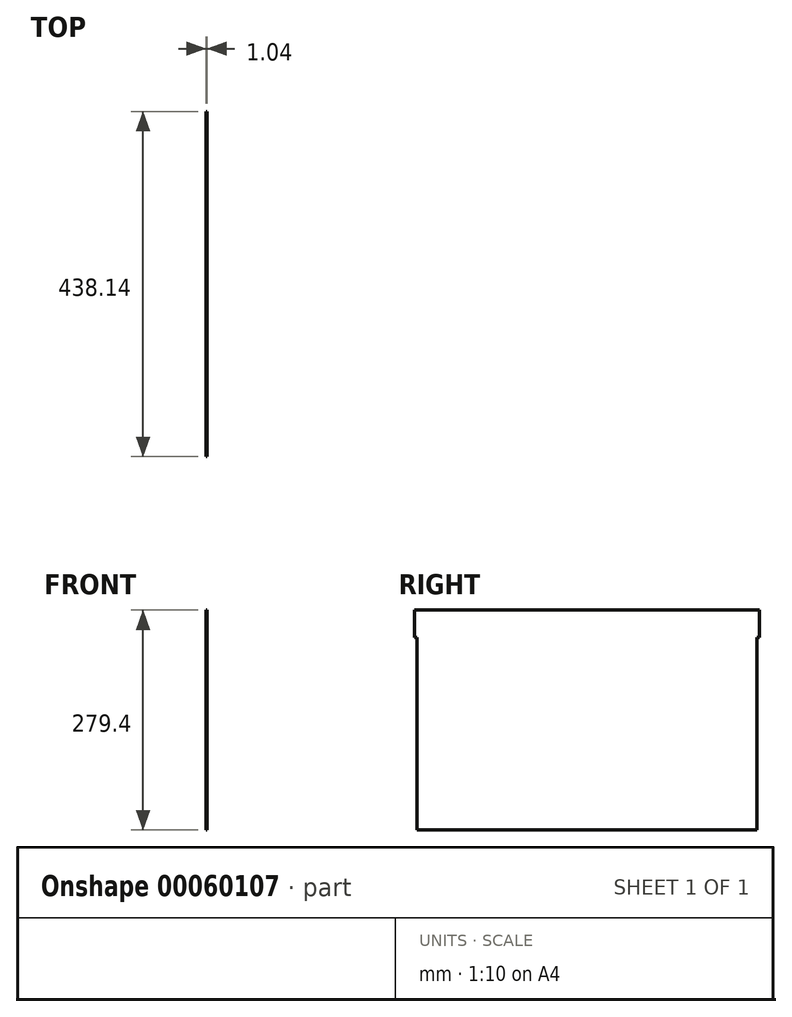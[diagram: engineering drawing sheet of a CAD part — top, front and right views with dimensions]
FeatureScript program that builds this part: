
annotation { "Feature Type Name" : "Feature", "Feature Type Description" : "" }
export const myFeature = defineFeature(function(context is Context, id is Id, definition is map)
    precondition{}
    {
        {
            var Q0;
            Q0=qCreatedBy(makeId("Right.planeOp"),FACE);
            var sketch = newSketch(context, id + "F0", { "sketchPlane" : qUnion([Q0])});
            skLineSegment(sketch, "E0", {"start": v(-219.08, 127) * mm, "end": v(219.08, 127) * mm});
            skLineSegment(sketch, "E1", {"start": v(219.07, 127) * mm, "end": v(219.07, 92.07) * mm});
            skLineSegment(sketch, "E2", {"start": v(219.07, 92.08) * mm, "end": v(215.9, 92.08) * mm});
            skLineSegment(sketch, "E3", {"start": v(215.9, 92.07) * mm, "end": v(215.9, -152.4) * mm});
            skLineSegment(sketch, "E4", {"start": v(215.9, -152.4) * mm, "end": v(-215.9, -152.4) * mm});
            skLineSegment(sketch, "E5", {"start": v(-215.9, -152.4) * mm, "end": v(-215.9, 92.07) * mm});
            skLineSegment(sketch, "E6", {"start": v(-215.9, 92.07) * mm, "end": v(-219.07, 92.07) * mm});
            skLineSegment(sketch, "E7", {"start": v(-219.07, 92.07) * mm, "end": v(-219.07, 127) * mm});
            skLineSegment(sketch, "E8", {"start": v(0, 0) * mm, "end": v(0, 127) * mm, "construction": true});
            skSolve(sketch);
        }
        {
            var Q0;
            Q0 = qSketchRegion(id + "F0", true);
            extrude(context, id + "F1", {"entities" : qUnion([Q0]), "depth" : (26 + 3 / 8) / 50.8 * mm, "hasSecondDirection" : true, "secondDirectionOppositeDirection" : true, "secondDirectionDepth" : (26 + 3 / 8) / 50.8 * mm});
        }
        {
            var Q0;
            Q0=makeQuery(id+"F1.opExtrude","SWEPT_FACE",FACE,{"disambiguationData":[OSD([sQuery(id+"F0.wireOp",EDGE,"E4")])]});
            var sketch = newSketch(context, id + "F2", { "sketchPlane" : qUnion([Q0])});
            skLineSegment(sketch, "E9.bottom", {"start": v(234.95, -215.9) * mm, "end": v(-234.95, -215.9) * mm, "construction": true});
            skLineSegment(sketch, "E9.top", {"start": v(234.95, 215.9) * mm, "end": v(-234.95, 215.9) * mm, "construction": true});
            skLineSegment(sketch, "E9.left", {"start": v(234.95, -215.9) * mm, "end": v(234.95, 215.9) * mm, "construction": true});
            skLineSegment(sketch, "E9.right", {"start": v(-234.95, -215.9) * mm, "end": v(-234.95, 215.9) * mm, "construction": true});
            skLineSegment(sketch, "E10", {"start": v(0, 0) * mm, "end": v(0, -215.9) * mm, "construction": true});
            skLineSegment(sketch, "E11", {"start": v(0, 0) * mm, "end": v(234.95, 0) * mm, "construction": true});
            skLineSegment(sketch, "E12.bottom", {"start": v(-334.96, -215.9) * mm, "end": v(-234.95, -215.9) * mm});
            skLineSegment(sketch, "E12.top", {"start": v(-334.96, 215.9) * mm, "end": v(-234.95, 215.9) * mm});
            skLineSegment(sketch, "E12.left", {"start": v(-334.96, -215.9) * mm, "end": v(-334.96, 215.9) * mm});
            skLineSegment(sketch, "E12.right", {"start": v(-234.95, -215.9) * mm, "end": v(-234.95, 215.9) * mm});
            skLineSegment(sketch, "E13.bottom", {"start": v(234.95, -215.9) * mm, "end": v(334.96, -215.9) * mm});
            skLineSegment(sketch, "E13.top", {"start": v(234.95, 215.9) * mm, "end": v(334.96, 215.9) * mm});
            skLineSegment(sketch, "E13.left", {"start": v(234.95, -215.9) * mm, "end": v(234.95, 215.9) * mm});
            skLineSegment(sketch, "E13.right", {"start": v(334.96, -215.9) * mm, "end": v(334.96, 215.9) * mm});
            skSolve(sketch);
        }
        {
            var Q0;
            Q0 = qSketchRegion(id + "F2", true);
            var Q1;
            Q1=makeQuery(id+"F1.opExtrude","SWEPT_FACE",FACE,{"disambiguationData":[OSD([sQuery(id+"F0.wireOp",EDGE,"E2")])]});
            extrude(context, id + "F3", {"entities" : qUnion([Q0]), "operationType" : NewBodyOperationType.REMOVE, "endBound" : BoundingType.UP_TO_SURFACE, "oppositeDirection" : true, "endBoundEntityFace" : qUnion([Q1]), "depth" : 25.4 * mm});
        }
    });
